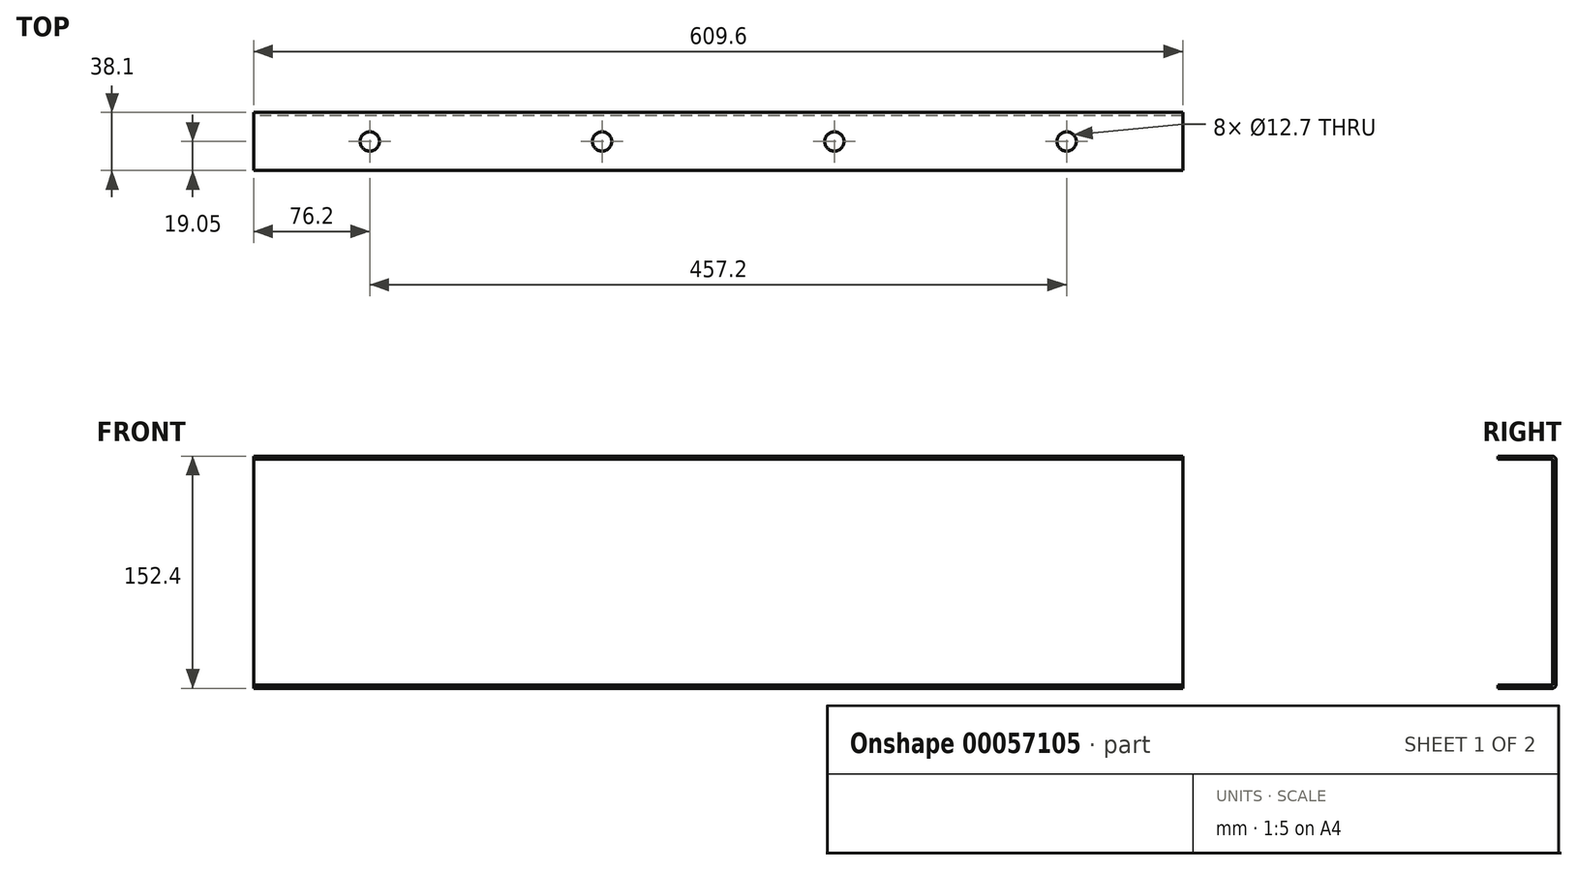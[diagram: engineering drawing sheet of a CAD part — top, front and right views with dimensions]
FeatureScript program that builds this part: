
annotation { "Feature Type Name" : "Feature", "Feature Type Description" : "" }
export const myFeature = defineFeature(function(context is Context, id is Id, definition is map)
    precondition{}
    {
        {
            var Q0;
            Q0=qCreatedBy(makeId("Top.planeOp"),FACE);
            var sketch = newSketch(context, id + "F0", { "sketchPlane" : qUnion([Q0])});
            skCircle(sketch, "E0", {"center": v(0, 0) * mm, "radius": 6.35 * mm});
            skLineSegment(sketch, "E1", {"start": v(0, 19.05) * mm, "end": v(0, -19.05) * mm, "construction": true});
            skCircle(sketch, "E2.1.0.0", {"center": v(152.4, 0) * mm, "radius": 6.35 * mm});
            skLineSegment(sketch, "E2.1.0.1", {"start": v(152.4, 19.05) * mm, "end": v(152.4, -19.05) * mm, "construction": true});
            skCircle(sketch, "E2.2.0.0", {"center": v(304.8, 0) * mm, "radius": 6.35 * mm});
            skLineSegment(sketch, "E2.2.0.1", {"start": v(304.8, 19.05) * mm, "end": v(304.8, -19.05) * mm, "construction": true});
            skCircle(sketch, "E2.3.0.0", {"center": v(457.2, 0) * mm, "radius": 6.35 * mm});
            skLineSegment(sketch, "E2.3.0.1", {"start": v(457.2, 19.05) * mm, "end": v(457.2, -19.05) * mm, "construction": true});
            skLineSegment(sketch, "E2.direction1", {"start": v(0, 0) * mm, "end": v(152.4, 0) * mm, "construction": true});
            skLineSegment(sketch, "E3", {"start": v(-76.2, 19.05) * mm, "end": v(533.4, 19.05) * mm});
            skLineSegment(sketch, "E4.MirrorCS", {"start": v(-76.2, -19.05) * mm, "end": v(533.4, -19.05) * mm});
            skLineSegment(sketch, "E5", {"start": v(-76.2, -19.05) * mm, "end": v(-76.2, 19.05) * mm});
            skLineSegment(sketch, "E6", {"start": v(533.4, -19.05) * mm, "end": v(533.4, 19.05) * mm});
            skSolve(sketch);
        }
        {
            var Q0;
            Q0=makeQuery(id+"F0.imprint","IMPRINT",FACE,{"disambiguationData":[TD([[makeQuery(id+"F0.imprint","IMPRINT",EDGE,{"derivedFrom":sQuery(id+"F0.wireOp",EDGE,"E0")}),-1.0]])]});
            extrude(context, id + "F1", {"entities" : qUnion([Q0]), "oppositeDirection" : true, "depth" : 152.4 * mm});
        }
        {
            var Q0;
            Q0=makeQuery(id+"F1.opExtrude","CAP_EDGE",EDGE,{"disambiguationData":[OSD([sQuery(id+"F0.wireOp",EDGE,"E3")])],"isStart":true});
            var Q1;
            Q1=makeQuery(id+"F1.opExtrude","CAP_EDGE",EDGE,{"disambiguationData":[OSD([sQuery(id+"F0.wireOp",EDGE,"E3")])],"isStart":false});
            fillet(context, id + "F2", {"entities" : qUnion([Q0, Q1]), "radius" : 2.54 * mm, "tangentPropagation" : true, "allowEdgeOverflow" : false});
        }
        {
            var Q0;
            Q0=makeQuery(id+"F1.opExtrude","SWEPT_FACE",FACE,{"disambiguationData":[OSD([sQuery(id+"F0.wireOp",EDGE,"E5")])]});
            var sketch = newSketch(context, id + "F3", { "sketchPlane" : qUnion([Q0])});
            skLineSegment(sketch, "E7.0", {"start": v(19.05, -150.28) * mm, "end": v(-16.51, -150.28) * mm});
            skLineSegment(sketch, "E7.1", {"start": v(19.05, -2.12) * mm, "end": v(-16.51, -2.12) * mm});
            skArc(sketch, "E7.2", {"start": v(-16.51, -2.12) * mm, "mid": v(-16.8, -2.24) * mm, "end": v(-16.93, -2.54) * mm});
            skLineSegment(sketch, "E7.3", {"start": v(-16.93, -149.86) * mm, "end": v(-16.93, -2.54) * mm});
            skArc(sketch, "E7.4", {"start": v(-16.93, -149.86) * mm, "mid": v(-16.8, -150.16) * mm, "end": v(-16.51, -150.28) * mm});
            skLineSegment(sketch, "E8", {"start": v(19.05, -2.12) * mm, "end": v(19.05, -150.28) * mm});
            skSolve(sketch);
        }
        {
            var Q0;
            Q0=makeQuery(id+"F3.imprint","IMPRINT",FACE,{"disambiguationData":[TD([[makeQuery(id+"F3.imprint","IMPRINT",EDGE,{"derivedFrom":sQuery(id+"F3.wireOp",EDGE,"E7.0")}),-1.0]])]});
            var Q1;
            Q1=makeQuery(id+"F1.opExtrude","SWEPT_FACE",FACE,{"disambiguationData":[OSD([sQuery(id+"F0.wireOp",EDGE,"E6")])]});
            extrude(context, id + "F4", {"entities" : qUnion([Q0]), "operationType" : NewBodyOperationType.REMOVE, "endBound" : BoundingType.UP_TO_SURFACE, "oppositeDirection" : true, "endBoundEntityFace" : qUnion([Q1]), "depth" : 25.4 * mm});
        }
    });
